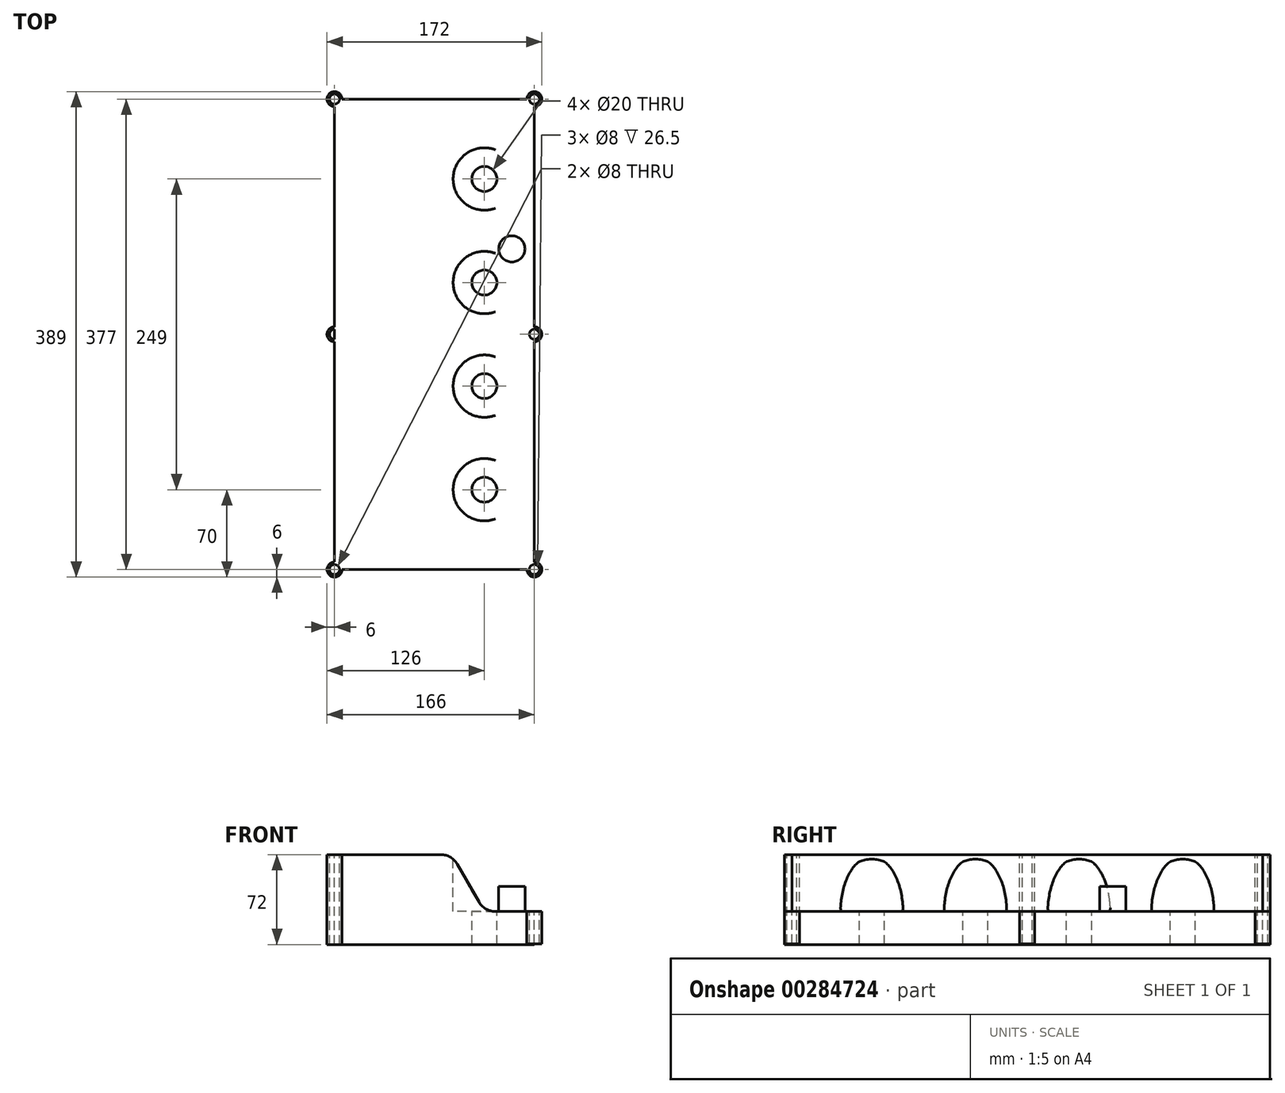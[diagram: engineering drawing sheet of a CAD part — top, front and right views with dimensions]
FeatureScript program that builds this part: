
annotation { "Feature Type Name" : "Feature", "Feature Type Description" : "" }
export const myFeature = defineFeature(function(context is Context, id is Id, definition is map)
    precondition{}
    {
        {
            var Q0;
            Q0=qCreatedBy(makeId("Front.planeOp"),FACE);
            var sketch = newSketch(context, id + "F0", { "sketchPlane" : qUnion([Q0])});
            skLineSegment(sketch, "E0", {"start": v(0, 0) * mm, "end": v(-160, 0) * mm});
            skLineSegment(sketch, "E1", {"start": v(-160, 0) * mm, "end": v(-160, 72) * mm});
            skLineSegment(sketch, "E2", {"start": v(-160, 72) * mm, "end": v(-40, 72) * mm, "construction": true});
            skLineSegment(sketch, "E3", {"start": v(0, 0) * mm, "end": v(0, 26.5) * mm});
            skLineSegment(sketch, "E4", {"start": v(0, 26.5) * mm, "end": v(-40, 26.5) * mm});
            skLineSegment(sketch, "E5", {"start": v(-40, 26.5) * mm, "end": v(-40, 72) * mm, "construction": true});
            skPoint(sketch, "E6", {"position": v(-40, 72) * mm});
            skPoint(sketch, "E7", {"position": v(-66, 72) * mm});
            skLineSegment(sketch, "E8", {"start": v(-66, 72) * mm, "end": v(-40, 26.5) * mm});
            skLineSegment(sketch, "E9", {"start": v(-160, 72) * mm, "end": v(-66, 72) * mm});
            skSolve(sketch);
        }
        {
            var Q0;
            Q0=qSketchRegion(id+"F0",true);
            extrude(context, id + "F1", {"entities" : qUnion([Q0]), "depth" : 377 * mm});
        }
        {
            var Q0;
            Q0=makeQuery(id+"F1.opExtrude","SWEPT_FACE",FACE,{"disambiguationData":[OSD([sQuery(id+"F0.wireOp",EDGE,"E4")])]});
            var sketch = newSketch(context, id + "F2", { "sketchPlane" : qUnion([Q0])});
            skCircle(sketch, "E10", {"center": v(0, 0) * mm, "radius": 6 * mm});
            skCircle(sketch, "E11", {"center": v(0, 0) * mm, "radius": 4 * mm});
            skCircle(sketch, "E12", {"center": v(0, -377) * mm, "radius": 6 * mm});
            skCircle(sketch, "E13", {"center": v(0, -377) * mm, "radius": 4 * mm});
            skLineSegment(sketch, "E14.0", {"start": v(-40, -377) * mm, "end": v(-40, 0) * mm});
            skPoint(sketch, "E15", {"position": v(-40, -377) * mm});
            skPoint(sketch, "E16", {"position": v(-40, -313) * mm});
            skPoint(sketch, "E17", {"position": v(-40, -230) * mm});
            skPoint(sketch, "E18", {"position": v(-40, -147) * mm});
            skPoint(sketch, "E19", {"position": v(-40, -64) * mm});
            skCircle(sketch, "E20", {"center": v(-40, -313) * mm, "radius": 10 * mm});
            skCircle(sketch, "E21", {"center": v(-40, -230) * mm, "radius": 10 * mm});
            skCircle(sketch, "E22", {"center": v(-40, -147) * mm, "radius": 10 * mm});
            skCircle(sketch, "E23", {"center": v(-40, -64) * mm, "radius": 10 * mm});
            skPoint(sketch, "E24", {"position": v(-18, -120) * mm});
            skCircle(sketch, "E25", {"center": v(-18, -120) * mm, "radius": 10.5 * mm});
            skPoint(sketch, "E26", {"position": v(0, -188.5) * mm});
            skCircle(sketch, "E27", {"center": v(0, -188.5) * mm, "radius": 6 * mm});
            skCircle(sketch, "E28", {"center": v(0, -188.5) * mm, "radius": 4 * mm});
            skSolve(sketch);
        }
        {
            var Q0;
            Q0=qSketchRegion(id+"F2",true);
            extrude(context, id + "F3", {"entities" : qUnion([Q0]), "operationType" : NewBodyOperationType.ADD, "oppositeDirection" : true, "depth" : 26 * mm});
        }
        {
            var Q0;
            {var subQ0=sQuery(id+"F2.wireOp",EDGE,"E11");var subQ1=sQuery(id+"F0.wireOp",EDGE,"E4");var subQ2=makeQuery(id+"F1.opExtrude","CAP_EDGE",EDGE,{"disambiguationData":[OSD([subQ1])],"isStart":true});var subQ3=makeQuery(id+"F2.imprint","INTERSECT",VERTEX,{"derivedFrom":[subQ2,subQ0]});Q0=makeQuery(id+"F2.imprint","IMPRINT",FACE,{"disambiguationData":[TD([[makeQuery(id+"F2.imprint","IMPRINT",EDGE,{"disambiguationData":[TD([[subQ3,-1.0]])],"derivedFrom":subQ0}),1.0]])]});}
            var Q1;
            {var subQ0=sQuery(id+"F2.wireOp",EDGE,"E13");var subQ1=sQuery(id+"F0.wireOp",EDGE,"E4");var subQ2=makeQuery(id+"F1.opExtrude","CAP_EDGE",EDGE,{"disambiguationData":[OSD([subQ1])],"isStart":false});var subQ3=makeQuery(id+"F2.imprint","INTERSECT",VERTEX,{"derivedFrom":[subQ2,subQ0]});Q1=makeQuery(id+"F2.imprint","IMPRINT",FACE,{"disambiguationData":[TD([[makeQuery(id+"F2.imprint","IMPRINT",EDGE,{"disambiguationData":[TD([[subQ3,1.0]])],"derivedFrom":subQ0}),1.0]])]});}
            var Q2;
            {var subQ0=sQuery(id+"F2.wireOp",EDGE,"E28");var subQ1=makeQuery(id+"F1.opExtrude","SWEPT_EDGE",EDGE,{"disambiguationData":[OSD([sQuery(id+"F0.wireOp",EDGE,"E3"),sQuery(id+"F0.wireOp",EDGE,"E4")])]});var subQ2=makeQuery(id+"F2.imprint","INTERSECT",VERTEX,{"disambiguationData":[OD(0.0)],"derivedFrom":[subQ1,subQ0]});Q2=makeQuery(id+"F2.imprint","IMPRINT",FACE,{"disambiguationData":[TD([[makeQuery(id+"F2.imprint","IMPRINT",EDGE,{"disambiguationData":[TD([[subQ2,-1.0]])],"derivedFrom":subQ0}),1.0]])]});}
            extrude(context, id + "F4", {"entities" : qUnion([Q0, Q1, Q2]), "operationType" : NewBodyOperationType.REMOVE, "oppositeDirection" : true, "depth" : 27 * mm});
        }
        {
            var Q0;
            {var subQ0=sQuery(id+"F2.wireOp",EDGE,"E20");var subQ1=sQuery(id+"F2.wireOp",EDGE,"E14.0");var subQ2=makeQuery(id+"F2.imprint","INTERSECT",VERTEX,{"disambiguationData":[OD(0.0)],"derivedFrom":[subQ1,subQ0]});Q0=makeQuery(id+"F2.imprint","IMPRINT",FACE,{"disambiguationData":[TD([[makeQuery(id+"F2.imprint","IMPRINT",EDGE,{"disambiguationData":[TD([[subQ2,-1.0]])],"derivedFrom":subQ1}),1.0]])]});}
            var Q1;
            {var subQ0=sQuery(id+"F2.wireOp",EDGE,"E21");var subQ1=sQuery(id+"F2.wireOp",EDGE,"E14.0");var subQ2=makeQuery(id+"F2.imprint","INTERSECT",VERTEX,{"disambiguationData":[OD(0.0)],"derivedFrom":[subQ1,subQ0]});Q1=makeQuery(id+"F2.imprint","IMPRINT",FACE,{"disambiguationData":[TD([[makeQuery(id+"F2.imprint","IMPRINT",EDGE,{"disambiguationData":[TD([[subQ2,-1.0]])],"derivedFrom":subQ1}),1.0]])]});}
            var Q2;
            {var subQ0=sQuery(id+"F2.wireOp",EDGE,"E22");var subQ1=sQuery(id+"F2.wireOp",EDGE,"E14.0");var subQ2=makeQuery(id+"F2.imprint","INTERSECT",VERTEX,{"disambiguationData":[OD(0.0)],"derivedFrom":[subQ1,subQ0]});Q2=makeQuery(id+"F2.imprint","IMPRINT",FACE,{"disambiguationData":[TD([[makeQuery(id+"F2.imprint","IMPRINT",EDGE,{"disambiguationData":[TD([[subQ2,-1.0]])],"derivedFrom":subQ1}),1.0]])]});}
            var Q3;
            {var subQ0=sQuery(id+"F2.wireOp",EDGE,"E23");var subQ1=sQuery(id+"F2.wireOp",EDGE,"E14.0");var subQ2=makeQuery(id+"F2.imprint","INTERSECT",VERTEX,{"disambiguationData":[OD(0.0)],"derivedFrom":[subQ1,subQ0]});Q3=makeQuery(id+"F2.imprint","IMPRINT",FACE,{"disambiguationData":[TD([[makeQuery(id+"F2.imprint","IMPRINT",EDGE,{"disambiguationData":[TD([[subQ2,-1.0]])],"derivedFrom":subQ1}),1.0]])]});}
            var Q4;
            {var subQ0=sQuery(id+"F2.wireOp",EDGE,"E20");var subQ1=sQuery(id+"F2.wireOp",EDGE,"E14.0");var subQ2=makeQuery(id+"F2.imprint","INTERSECT",VERTEX,{"disambiguationData":[OD(0.0)],"derivedFrom":[subQ1,subQ0]});Q4=makeQuery(id+"F2.imprint","IMPRINT",FACE,{"disambiguationData":[TD([[makeQuery(id+"F2.imprint","IMPRINT",EDGE,{"disambiguationData":[TD([[subQ2,-1.0]])],"derivedFrom":subQ1}),-1.0]])]});}
            var Q5;
            {var subQ0=sQuery(id+"F2.wireOp",EDGE,"E21");var subQ1=sQuery(id+"F2.wireOp",EDGE,"E14.0");var subQ2=makeQuery(id+"F2.imprint","INTERSECT",VERTEX,{"disambiguationData":[OD(0.0)],"derivedFrom":[subQ1,subQ0]});Q5=makeQuery(id+"F2.imprint","IMPRINT",FACE,{"disambiguationData":[TD([[makeQuery(id+"F2.imprint","IMPRINT",EDGE,{"disambiguationData":[TD([[subQ2,-1.0]])],"derivedFrom":subQ1}),-1.0]])]});}
            var Q6;
            {var subQ0=sQuery(id+"F2.wireOp",EDGE,"E22");var subQ1=sQuery(id+"F2.wireOp",EDGE,"E14.0");var subQ2=makeQuery(id+"F2.imprint","INTERSECT",VERTEX,{"disambiguationData":[OD(0.0)],"derivedFrom":[subQ1,subQ0]});Q6=makeQuery(id+"F2.imprint","IMPRINT",FACE,{"disambiguationData":[TD([[makeQuery(id+"F2.imprint","IMPRINT",EDGE,{"disambiguationData":[TD([[subQ2,-1.0]])],"derivedFrom":subQ1}),-1.0]])]});}
            var Q7;
            {var subQ0=sQuery(id+"F2.wireOp",EDGE,"E23");var subQ1=sQuery(id+"F2.wireOp",EDGE,"E14.0");var subQ2=makeQuery(id+"F2.imprint","INTERSECT",VERTEX,{"disambiguationData":[OD(0.0)],"derivedFrom":[subQ1,subQ0]});Q7=makeQuery(id+"F2.imprint","IMPRINT",FACE,{"disambiguationData":[TD([[makeQuery(id+"F2.imprint","IMPRINT",EDGE,{"disambiguationData":[TD([[subQ2,-1.0]])],"derivedFrom":subQ1}),-1.0]])]});}
            extrude(context, id + "F5", {"entities" : qUnion([Q0, Q1, Q2, Q3, Q4, Q5, Q6, Q7]), "operationType" : NewBodyOperationType.REMOVE, "endBound" : BoundingType.SYMMETRIC, "oppositeDirection" : true, "depth" : 55 * mm});
        }
        {
            var Q0;
            Q0=makeQuery(id+"F1.opExtrude","SWEPT_FACE",FACE,{"disambiguationData":[OSD([sQuery(id+"F0.wireOp",EDGE,"E9")])]});
            var sketch = newSketch(context, id + "F6", { "sketchPlane" : qUnion([Q0])});
            skCircle(sketch, "E29", {"center": v(-160, 0) * mm, "radius": 6 * mm});
            skCircle(sketch, "E30", {"center": v(-160, 0) * mm, "radius": 4 * mm});
            skCircle(sketch, "E31", {"center": v(-160, -377) * mm, "radius": 6 * mm});
            skCircle(sketch, "E32", {"center": v(-160, -377) * mm, "radius": 4 * mm});
            skArc(sketch, "E33.0", {"start": v(-40, -54) * mm, "mid": v(-50, -64) * mm, "end": v(-40, -74) * mm});
            skArc(sketch, "E34.0", {"start": v(-40, -137) * mm, "mid": v(-50, -147) * mm, "end": v(-40, -157) * mm});
            skArc(sketch, "E35.0", {"start": v(-40, -220) * mm, "mid": v(-50, -230) * mm, "end": v(-40, -240) * mm});
            skArc(sketch, "E36.0", {"start": v(-40, -303) * mm, "mid": v(-50, -313) * mm, "end": v(-40, -323) * mm});
            skArc(sketch, "E37", {"start": v(-40, -39) * mm, "mid": v(-65, -64) * mm, "end": v(-40, -89) * mm});
            skArc(sketch, "E38", {"start": v(-40, -122) * mm, "mid": v(-65, -147) * mm, "end": v(-40, -172) * mm});
            skArc(sketch, "E39", {"start": v(-40, -205) * mm, "mid": v(-65, -230) * mm, "end": v(-40, -255) * mm});
            skArc(sketch, "E40", {"start": v(-40, -288) * mm, "mid": v(-65, -313) * mm, "end": v(-40, -338) * mm});
            skLineSegment(sketch, "E41", {"start": v(-40, -172) * mm, "end": v(-40, -157) * mm});
            skLineSegment(sketch, "E42", {"start": v(-40, -205) * mm, "end": v(-40, -220) * mm});
            skLineSegment(sketch, "E43", {"start": v(-40, -288) * mm, "end": v(-40, -303) * mm});
            skLineSegment(sketch, "E44", {"start": v(-40, -89) * mm, "end": v(-40, -74) * mm});
            skLineSegment(sketch, "E45", {"start": v(-40, -39) * mm, "end": v(-40, -54) * mm});
            skLineSegment(sketch, "E46.trimOffspring", {"start": v(-40, -137) * mm, "end": v(-40, -122) * mm});
            skLineSegment(sketch, "E47.trimOffspring", {"start": v(-40, -240) * mm, "end": v(-40, -255) * mm});
            skLineSegment(sketch, "E48.trimOffspring", {"start": v(-40, -323) * mm, "end": v(-40, -338) * mm});
            skCircle(sketch, "E49", {"center": v(-160, -188.5) * mm, "radius": 6 * mm});
            skCircle(sketch, "E50", {"center": v(-160, -188.5) * mm, "radius": 4 * mm});
            skSolve(sketch);
        }
        {
            var Q0;
            Q0=qSketchRegion(id+"F6",true);
            extrude(context, id + "F7", {"entities" : qUnion([Q0]), "operationType" : NewBodyOperationType.ADD, "oppositeDirection" : true, "depth" : 72 * mm});
        }
        {
            var Q0;
            {var subQ0=sQuery(id+"F6.wireOp",EDGE,"E32");var subQ1=sQuery(id+"F0.wireOp",EDGE,"E9");var subQ2=makeQuery(id+"F1.opExtrude","CAP_EDGE",EDGE,{"disambiguationData":[OSD([subQ1])],"isStart":false});var subQ3=makeQuery(id+"F6.imprint","INTERSECT",VERTEX,{"derivedFrom":[subQ2,subQ0]});Q0=makeQuery(id+"F6.imprint","IMPRINT",FACE,{"disambiguationData":[TD([[makeQuery(id+"F6.imprint","IMPRINT",EDGE,{"disambiguationData":[TD([[subQ3,-1.0]])],"derivedFrom":subQ0}),1.0]])]});}
            var Q1;
            {var subQ0=sQuery(id+"F6.wireOp",EDGE,"E30");var subQ1=sQuery(id+"F0.wireOp",EDGE,"E9");var subQ2=makeQuery(id+"F1.opExtrude","CAP_EDGE",EDGE,{"disambiguationData":[OSD([subQ1])],"isStart":true});var subQ3=makeQuery(id+"F6.imprint","INTERSECT",VERTEX,{"derivedFrom":[subQ2,subQ0]});Q1=makeQuery(id+"F6.imprint","IMPRINT",FACE,{"disambiguationData":[TD([[makeQuery(id+"F6.imprint","IMPRINT",EDGE,{"disambiguationData":[TD([[subQ3,1.0]])],"derivedFrom":subQ0}),1.0]])]});}
            var Q2;
            {var subQ0=sQuery(id+"F6.wireOp",EDGE,"E50");var subQ1=makeQuery(id+"F1.opExtrude","SWEPT_EDGE",EDGE,{"disambiguationData":[OSD([sQuery(id+"F0.wireOp",EDGE,"E1"),sQuery(id+"F0.wireOp",EDGE,"E9")])]});var subQ2=makeQuery(id+"F6.imprint","INTERSECT",VERTEX,{"disambiguationData":[OD(0.0)],"derivedFrom":[subQ1,subQ0]});Q2=makeQuery(id+"F6.imprint","IMPRINT",FACE,{"disambiguationData":[TD([[makeQuery(id+"F6.imprint","IMPRINT",EDGE,{"disambiguationData":[TD([[subQ2,1.0]])],"derivedFrom":subQ0}),1.0]])]});}
            extrude(context, id + "F8", {"entities" : qUnion([Q0, Q1, Q2]), "operationType" : NewBodyOperationType.REMOVE, "oppositeDirection" : true, "depth" : 72 * mm});
        }
        {
            var Q0;
            Q0=makeQuery(id+"F2.imprint","IMPRINT",FACE,{"disambiguationData":[TD([[makeQuery(id+"F2.imprint","IMPRINT",EDGE,{"derivedFrom":sQuery(id+"F2.wireOp",EDGE,"E25")}),1.0]])]});
            extrude(context, id + "F9", {"entities" : qUnion([Q0]), "operationType" : NewBodyOperationType.ADD, "depth" : 20 * mm});
        }
        {
            var Q0;
            Q0=makeQuery(id+"F6.imprint","IMPRINT",FACE,{"disambiguationData":[TD([[makeQuery(id+"F6.imprint","IMPRINT",EDGE,{"derivedFrom":sQuery(id+"F6.wireOp",EDGE,"E33.0")}),-1.0]])]});
            var Q1;
            Q1=makeQuery(id+"F6.imprint","IMPRINT",FACE,{"disambiguationData":[TD([[makeQuery(id+"F6.imprint","IMPRINT",EDGE,{"derivedFrom":sQuery(id+"F6.wireOp",EDGE,"E34.0")}),-1.0]])]});
            var Q2;
            Q2=makeQuery(id+"F6.imprint","IMPRINT",FACE,{"disambiguationData":[TD([[makeQuery(id+"F6.imprint","IMPRINT",EDGE,{"derivedFrom":sQuery(id+"F6.wireOp",EDGE,"E35.0")}),-1.0]])]});
            var Q3;
            Q3=makeQuery(id+"F6.imprint","IMPRINT",FACE,{"disambiguationData":[TD([[makeQuery(id+"F6.imprint","IMPRINT",EDGE,{"derivedFrom":sQuery(id+"F6.wireOp",EDGE,"E36.0")}),-1.0]])]});
            extrude(context, id + "F10", {"entities" : qUnion([Q0, Q1, Q2, Q3]), "operationType" : NewBodyOperationType.REMOVE, "oppositeDirection" : true, "depth" : 45.5 * mm});
        }
        {
            var Q0;
            Q0=makeQuery(id+"F1.opExtrude","SWEPT_EDGE",EDGE,{"disambiguationData":[OSD([sQuery(id+"F0.wireOp",EDGE,"E8"),sQuery(id+"F0.wireOp",EDGE,"E9")])]});
            var Q1;
            {var subQ0=makeQuery(id+"F3.opExtrude","CAP_FACE",FACE,{"disambiguationData":[OSD([sQuery(id+"F2.wireOp",EDGE,"E10"),sQuery(id+"F2.wireOp",EDGE,"E11")])],"isStart":true});var subQ1=sQuery(id+"F0.wireOp",EDGE,"E8");var subQ2=makeQuery(id+"F1.opExtrude","SWEPT_FACE",FACE,{"disambiguationData":[OSD([subQ1])]});var subQ3=sQuery(id+"F0.wireOp",EDGE,"E4");var subQ4=makeQuery(id+"F1.opExtrude","SWEPT_FACE",FACE,{"disambiguationData":[OSD([subQ3])]});var subQ5=makeQuery(id+"F1.opExtrude","CAP_FACE",FACE,{"disambiguationData":[OSD([sQuery(id+"F0.wireOp",EDGE,"E0"),sQuery(id+"F0.wireOp",EDGE,"E1"),sQuery(id+"F0.wireOp",EDGE,"E3"),subQ3,subQ1,sQuery(id+"F0.wireOp",EDGE,"E9")])],"isStart":false});var subQ6=makeQuery(id+"F3.opExtrude","CAP_FACE",FACE,{"disambiguationData":[OSD([sQuery(id+"F2.wireOp",EDGE,"E12"),sQuery(id+"F2.wireOp",EDGE,"E13")])],"isStart":true});var subQ7=sQuery(id+"F2.wireOp",EDGE,"E20");Q1=makeQuery(id+"F7.boolean.opBoolean","SPLIT",EDGE,{"disambiguationData":[TD([subQ5])],"derivedFrom":makeQuery(id+"F5.boolean.opBoolean","SPLIT",EDGE,{"disambiguationData":[TD([subQ5,subQ4,subQ2,subQ0,subQ6,makeQuery(id+"F5.opExtrude","SWEPT_FACE",FACE,{"disambiguationData":[OSD([subQ7])]})])],"derivedFrom":makeQuery(id+"F3.boolean.opBoolean","INTERSECT",EDGE,{"derivedFrom":[makeQuery(id+"F3.opExtrude","CAP_FACE",FACE,{"disambiguationData":[OSD([subQ7])],"isStart":true}),makeQuery(id+"F3.opExtrude","CAP_FACE",FACE,{"disambiguationData":[OSD([sQuery(id+"F2.wireOp",EDGE,"E21")])],"isStart":true}),makeQuery(id+"F3.opExtrude","CAP_FACE",FACE,{"disambiguationData":[OSD([sQuery(id+"F2.wireOp",EDGE,"E22")])],"isStart":true}),makeQuery(id+"F3.opExtrude","CAP_FACE",FACE,{"disambiguationData":[OSD([sQuery(id+"F2.wireOp",EDGE,"E23")])],"isStart":true})]})})});}
            var Q2;
            {var subQ0=makeQuery(id+"F3.opExtrude","CAP_FACE",FACE,{"disambiguationData":[OSD([sQuery(id+"F2.wireOp",EDGE,"E10"),sQuery(id+"F2.wireOp",EDGE,"E11")])],"isStart":true});var subQ1=makeQuery(id+"F1.opExtrude","SWEPT_FACE",FACE,{"disambiguationData":[OSD([sQuery(id+"F0.wireOp",EDGE,"E8")])]});var subQ2=makeQuery(id+"F3.opExtrude","CAP_FACE",FACE,{"disambiguationData":[OSD([sQuery(id+"F2.wireOp",EDGE,"E12"),sQuery(id+"F2.wireOp",EDGE,"E13")])],"isStart":true});var subQ3=makeQuery(id+"F1.opExtrude","SWEPT_FACE",FACE,{"disambiguationData":[OSD([sQuery(id+"F0.wireOp",EDGE,"E4")])]});var subQ4=sQuery(id+"F2.wireOp",EDGE,"E20");var subQ5=sQuery(id+"F2.wireOp",EDGE,"E21");Q2=makeQuery(id+"F7.boolean.opBoolean","SPLIT",EDGE,{"disambiguationData":[TD([subQ3,subQ1,subQ0,subQ2,makeQuery(id+"F7.opExtrude","SWEPT_FACE",FACE,{"disambiguationData":[OSD([sQuery(id+"F6.wireOp",EDGE,"E39")])]}),makeQuery(id+"F7.opExtrude","SWEPT_FACE",FACE,{"disambiguationData":[OSD([sQuery(id+"F6.wireOp",EDGE,"E40")])]}),makeQuery(id+"F7.opExtrude","SWEPT_FACE",FACE,{"disambiguationData":[OSD([sQuery(id+"F6.wireOp",EDGE,"E43")])]}),makeQuery(id+"F7.opExtrude","SWEPT_FACE",FACE,{"disambiguationData":[OSD([sQuery(id+"F6.wireOp",EDGE,"E47.trimOffspring")])]})])],"derivedFrom":makeQuery(id+"F5.boolean.opBoolean","SPLIT",EDGE,{"disambiguationData":[TD([subQ3,subQ1,subQ0,subQ2,makeQuery(id+"F5.opExtrude","SWEPT_FACE",FACE,{"disambiguationData":[OSD([subQ4])]}),makeQuery(id+"F5.opExtrude","SWEPT_FACE",FACE,{"disambiguationData":[OSD([subQ5])]})])],"derivedFrom":makeQuery(id+"F3.boolean.opBoolean","INTERSECT",EDGE,{"derivedFrom":[makeQuery(id+"F3.opExtrude","CAP_FACE",FACE,{"disambiguationData":[OSD([subQ4])],"isStart":true}),makeQuery(id+"F3.opExtrude","CAP_FACE",FACE,{"disambiguationData":[OSD([subQ5])],"isStart":true}),makeQuery(id+"F3.opExtrude","CAP_FACE",FACE,{"disambiguationData":[OSD([sQuery(id+"F2.wireOp",EDGE,"E22")])],"isStart":true}),makeQuery(id+"F3.opExtrude","CAP_FACE",FACE,{"disambiguationData":[OSD([sQuery(id+"F2.wireOp",EDGE,"E23")])],"isStart":true})]})})});}
            var Q3;
            {var subQ0=makeQuery(id+"F3.opExtrude","CAP_FACE",FACE,{"disambiguationData":[OSD([sQuery(id+"F2.wireOp",EDGE,"E10"),sQuery(id+"F2.wireOp",EDGE,"E11")])],"isStart":true});var subQ1=makeQuery(id+"F1.opExtrude","SWEPT_FACE",FACE,{"disambiguationData":[OSD([sQuery(id+"F0.wireOp",EDGE,"E8")])]});var subQ2=makeQuery(id+"F3.opExtrude","CAP_FACE",FACE,{"disambiguationData":[OSD([sQuery(id+"F2.wireOp",EDGE,"E12"),sQuery(id+"F2.wireOp",EDGE,"E13")])],"isStart":true});var subQ3=makeQuery(id+"F1.opExtrude","SWEPT_FACE",FACE,{"disambiguationData":[OSD([sQuery(id+"F0.wireOp",EDGE,"E4")])]});var subQ4=sQuery(id+"F2.wireOp",EDGE,"E21");var subQ5=sQuery(id+"F2.wireOp",EDGE,"E22");Q3=makeQuery(id+"F7.boolean.opBoolean","SPLIT",EDGE,{"disambiguationData":[TD([subQ3,subQ1,subQ0,subQ2,makeQuery(id+"F7.opExtrude","SWEPT_FACE",FACE,{"disambiguationData":[OSD([sQuery(id+"F6.wireOp",EDGE,"E38")])]}),makeQuery(id+"F7.opExtrude","SWEPT_FACE",FACE,{"disambiguationData":[OSD([sQuery(id+"F6.wireOp",EDGE,"E39")])]}),makeQuery(id+"F7.opExtrude","SWEPT_FACE",FACE,{"disambiguationData":[OSD([sQuery(id+"F6.wireOp",EDGE,"E41")])]}),makeQuery(id+"F7.opExtrude","SWEPT_FACE",FACE,{"disambiguationData":[OSD([sQuery(id+"F6.wireOp",EDGE,"E42")])]})])],"derivedFrom":makeQuery(id+"F5.boolean.opBoolean","SPLIT",EDGE,{"disambiguationData":[TD([subQ3,subQ1,subQ0,subQ2,makeQuery(id+"F5.opExtrude","SWEPT_FACE",FACE,{"disambiguationData":[OSD([subQ4])]}),makeQuery(id+"F5.opExtrude","SWEPT_FACE",FACE,{"disambiguationData":[OSD([subQ5])]})])],"derivedFrom":makeQuery(id+"F3.boolean.opBoolean","INTERSECT",EDGE,{"derivedFrom":[makeQuery(id+"F3.opExtrude","CAP_FACE",FACE,{"disambiguationData":[OSD([sQuery(id+"F2.wireOp",EDGE,"E20")])],"isStart":true}),makeQuery(id+"F3.opExtrude","CAP_FACE",FACE,{"disambiguationData":[OSD([subQ4])],"isStart":true}),makeQuery(id+"F3.opExtrude","CAP_FACE",FACE,{"disambiguationData":[OSD([subQ5])],"isStart":true}),makeQuery(id+"F3.opExtrude","CAP_FACE",FACE,{"disambiguationData":[OSD([sQuery(id+"F2.wireOp",EDGE,"E23")])],"isStart":true})]})})});}
            var Q4;
            {var subQ0=makeQuery(id+"F3.opExtrude","CAP_FACE",FACE,{"disambiguationData":[OSD([sQuery(id+"F2.wireOp",EDGE,"E10"),sQuery(id+"F2.wireOp",EDGE,"E11")])],"isStart":true});var subQ1=makeQuery(id+"F1.opExtrude","SWEPT_FACE",FACE,{"disambiguationData":[OSD([sQuery(id+"F0.wireOp",EDGE,"E8")])]});var subQ2=makeQuery(id+"F3.opExtrude","CAP_FACE",FACE,{"disambiguationData":[OSD([sQuery(id+"F2.wireOp",EDGE,"E12"),sQuery(id+"F2.wireOp",EDGE,"E13")])],"isStart":true});var subQ3=makeQuery(id+"F1.opExtrude","SWEPT_FACE",FACE,{"disambiguationData":[OSD([sQuery(id+"F0.wireOp",EDGE,"E4")])]});var subQ4=sQuery(id+"F2.wireOp",EDGE,"E22");var subQ5=sQuery(id+"F2.wireOp",EDGE,"E23");Q4=makeQuery(id+"F7.boolean.opBoolean","SPLIT",EDGE,{"disambiguationData":[TD([subQ3,subQ1,subQ0,subQ2,makeQuery(id+"F7.opExtrude","SWEPT_FACE",FACE,{"disambiguationData":[OSD([sQuery(id+"F6.wireOp",EDGE,"E37")])]}),makeQuery(id+"F7.opExtrude","SWEPT_FACE",FACE,{"disambiguationData":[OSD([sQuery(id+"F6.wireOp",EDGE,"E38")])]}),makeQuery(id+"F7.opExtrude","SWEPT_FACE",FACE,{"disambiguationData":[OSD([sQuery(id+"F6.wireOp",EDGE,"E44")])]}),makeQuery(id+"F7.opExtrude","SWEPT_FACE",FACE,{"disambiguationData":[OSD([sQuery(id+"F6.wireOp",EDGE,"E46.trimOffspring")])]})])],"derivedFrom":makeQuery(id+"F5.boolean.opBoolean","SPLIT",EDGE,{"disambiguationData":[TD([subQ3,subQ1,subQ0,subQ2,makeQuery(id+"F5.opExtrude","SWEPT_FACE",FACE,{"disambiguationData":[OSD([subQ4])]}),makeQuery(id+"F5.opExtrude","SWEPT_FACE",FACE,{"disambiguationData":[OSD([subQ5])]})])],"derivedFrom":makeQuery(id+"F3.boolean.opBoolean","INTERSECT",EDGE,{"derivedFrom":[makeQuery(id+"F3.opExtrude","CAP_FACE",FACE,{"disambiguationData":[OSD([sQuery(id+"F2.wireOp",EDGE,"E20")])],"isStart":true}),makeQuery(id+"F3.opExtrude","CAP_FACE",FACE,{"disambiguationData":[OSD([sQuery(id+"F2.wireOp",EDGE,"E21")])],"isStart":true}),makeQuery(id+"F3.opExtrude","CAP_FACE",FACE,{"disambiguationData":[OSD([subQ4])],"isStart":true}),makeQuery(id+"F3.opExtrude","CAP_FACE",FACE,{"disambiguationData":[OSD([subQ5])],"isStart":true})]})})});}
            var Q5;
            {var subQ0=sQuery(id+"F0.wireOp",EDGE,"E8");var subQ1=makeQuery(id+"F1.opExtrude","SWEPT_FACE",FACE,{"disambiguationData":[OSD([subQ0])]});var subQ2=sQuery(id+"F0.wireOp",EDGE,"E4");var subQ3=makeQuery(id+"F1.opExtrude","SWEPT_FACE",FACE,{"disambiguationData":[OSD([subQ2])]});var subQ4=makeQuery(id+"F3.opExtrude","CAP_FACE",FACE,{"disambiguationData":[OSD([sQuery(id+"F2.wireOp",EDGE,"E10"),sQuery(id+"F2.wireOp",EDGE,"E11")])],"isStart":true});var subQ5=makeQuery(id+"F1.opExtrude","CAP_FACE",FACE,{"disambiguationData":[OSD([sQuery(id+"F0.wireOp",EDGE,"E0"),sQuery(id+"F0.wireOp",EDGE,"E1"),sQuery(id+"F0.wireOp",EDGE,"E3"),subQ2,subQ0,sQuery(id+"F0.wireOp",EDGE,"E9")])],"isStart":true});var subQ6=makeQuery(id+"F3.opExtrude","CAP_FACE",FACE,{"disambiguationData":[OSD([sQuery(id+"F2.wireOp",EDGE,"E12"),sQuery(id+"F2.wireOp",EDGE,"E13")])],"isStart":true});var subQ7=sQuery(id+"F2.wireOp",EDGE,"E23");Q5=makeQuery(id+"F7.boolean.opBoolean","SPLIT",EDGE,{"disambiguationData":[TD([subQ5])],"derivedFrom":makeQuery(id+"F5.boolean.opBoolean","SPLIT",EDGE,{"disambiguationData":[TD([subQ5,subQ3,subQ1,subQ4,subQ6,makeQuery(id+"F5.opExtrude","SWEPT_FACE",FACE,{"disambiguationData":[OSD([subQ7])]})])],"derivedFrom":makeQuery(id+"F3.boolean.opBoolean","INTERSECT",EDGE,{"derivedFrom":[makeQuery(id+"F3.opExtrude","CAP_FACE",FACE,{"disambiguationData":[OSD([sQuery(id+"F2.wireOp",EDGE,"E20")])],"isStart":true}),makeQuery(id+"F3.opExtrude","CAP_FACE",FACE,{"disambiguationData":[OSD([sQuery(id+"F2.wireOp",EDGE,"E21")])],"isStart":true}),makeQuery(id+"F3.opExtrude","CAP_FACE",FACE,{"disambiguationData":[OSD([sQuery(id+"F2.wireOp",EDGE,"E22")])],"isStart":true}),makeQuery(id+"F3.opExtrude","CAP_FACE",FACE,{"disambiguationData":[OSD([subQ7])],"isStart":true})]})})});}
            fillet(context, id + "F11", {"entities" : qUnion([Q0, Q1, Q2, Q3, Q4, Q5]), "radius" : 15 * mm, "tangentPropagation" : true, "allowEdgeOverflow" : false});
        }
    });
